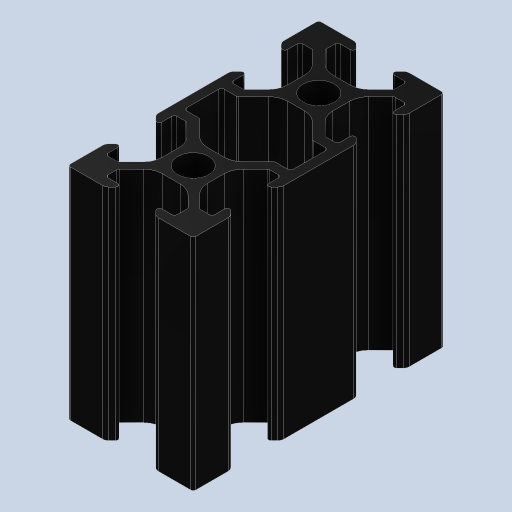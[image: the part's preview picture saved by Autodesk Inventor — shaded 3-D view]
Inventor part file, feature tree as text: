
AUTODESK INVENTOR PART (.ipt)
format: ipt  version: 2023 (Build 270158000, 158)  size: 362,496 bytes
history: native  units: mm
features: other x1, extrude x1, sketch x1
ambient origin geometry x8: Origin, YZ Plane, XZ Plane, XY Plane, X Axis, Y Axis, Z Axis, Center Point
bodies: Body1 (feature_tree)
feature tree (3):
  other  "Sólido1"
  extrude  "Extrusão1"  TaperAngle=45.0deg  [1 undecoded]
  sketch  "Esboço2"  dims[d137=4.5mm d138=45.0deg d139=6.4mm d141=1.5mm d142=1.5mm d145=0.4mm d146=6.5mm d147=45.0deg d148=1.0mm d151=20.0mm d152=20.0mm d153=5.2mm d154=7.4mm d155=13.6mm d156=3.0mm d157=135.0deg d158=3.0mm d159=5.0mm d160=5.0mm d161=0.4mm d162=35.0mm d163=0.0mm]
note: 1 required parameter value undecoded (feature->parameter linkage not recoverable at this tier; creation-order binding heuristic only, values carry confidence <= 0.55)
